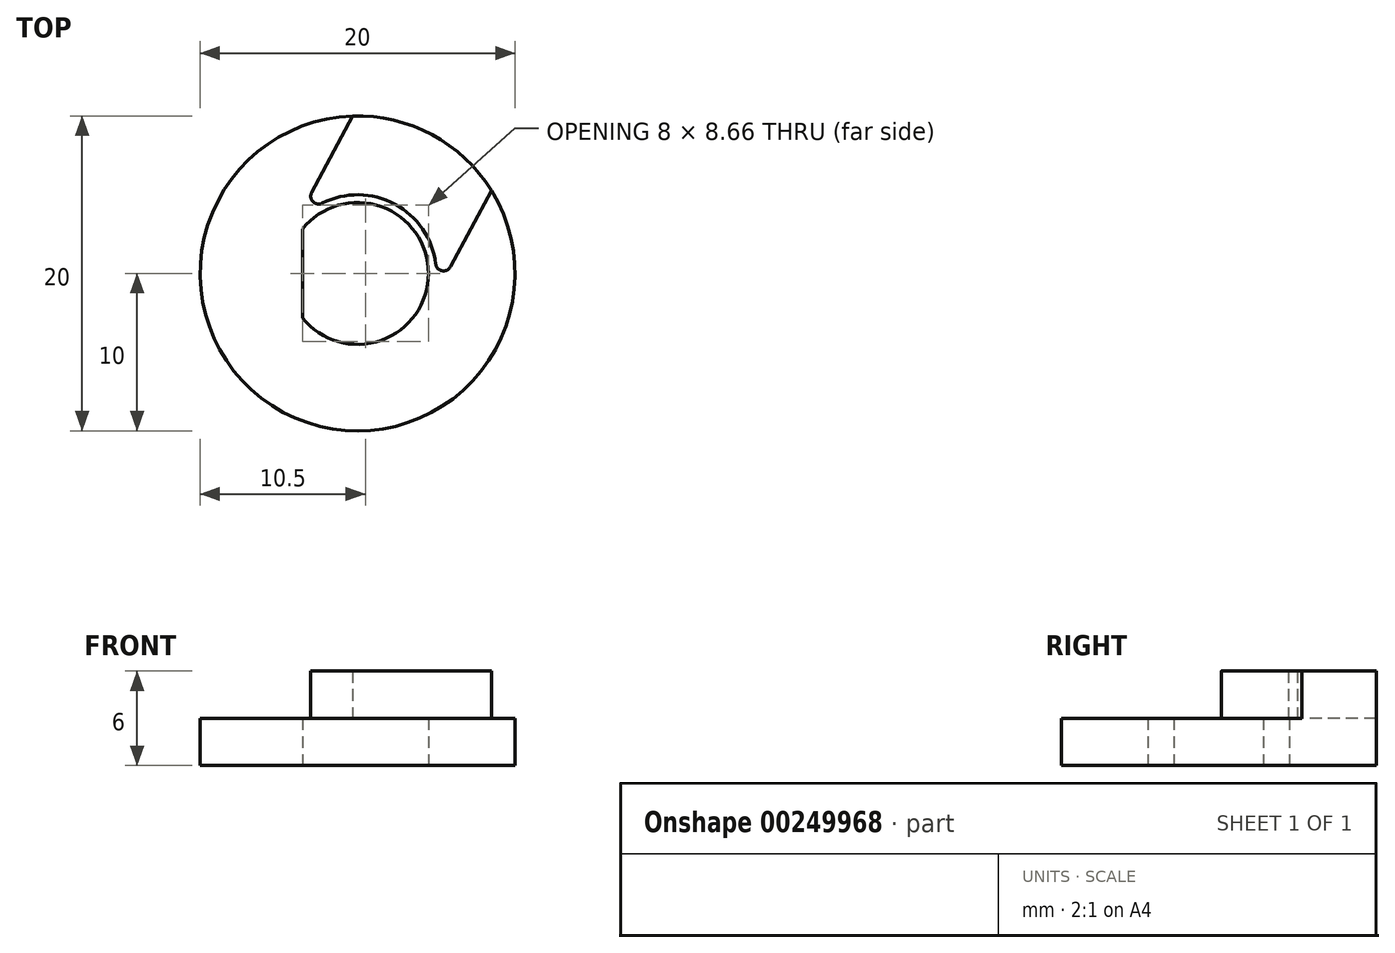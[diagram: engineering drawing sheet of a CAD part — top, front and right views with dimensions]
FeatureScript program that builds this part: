
annotation { "Feature Type Name" : "Feature", "Feature Type Description" : "" }
export const myFeature = defineFeature(function(context is Context, id is Id, definition is map)
    precondition{}
    {
        {
            var Q0;
            Q0=qCreatedBy(makeId("Top.planeOp"),FACE);
            var sketch = newSketch(context, id + "F0", { "sketchPlane" : qUnion([Q0])});
            skArc(sketch, "E0", {"start": v(-3.5, -2.83) * mm, "mid": v(4.5, 0) * mm, "end": v(-3.5, 2.83) * mm});
            skCircle(sketch, "E1", {"center": v(0, 0) * mm, "radius": 10 * mm});
            skLineSegment(sketch, "E2", {"start": v(-3.5, -2.83) * mm, "end": v(-3.5, 2.83) * mm});
            skPoint(sketch, "E3.start.orphan", {"position": v(4.5, 0) * mm});
            skArc(sketch, "E4", {"start": v(4.4, -2.36) * mm, "mid": v(2.36, 4.4) * mm, "end": v(-4.4, 2.36) * mm});
            skLineSegment(sketch, "E5", {"start": v(-4.4, 2.36) * mm, "end": v(-0.32, 10) * mm});
            skLineSegment(sketch, "E6", {"start": v(4.4, -2.36) * mm, "end": v(8.5, 5.28) * mm});
            skSolve(sketch);
        }
        {
            var Q0;
            Q0=makeQuery(id+"F0.imprint","IMPRINT",FACE,{"disambiguationData":[TD([[makeQuery(id+"F0.imprint","IMPRINT",EDGE,{"derivedFrom":sQuery(id+"F0.wireOp",EDGE,"E0")}),-1.0]])]});
            var Q1;
            Q1=makeQuery(id+"F0.imprint","IMPRINT",FACE,{"disambiguationData":[TD([[makeQuery(id+"F0.imprint","IMPRINT",EDGE,{"derivedFrom":sQuery(id+"F0.wireOp",EDGE,"E4")}),-1.0]])]});
            extrude(context, id + "F1", {"entities" : qUnion([Q0, Q1]), "depth" : 3 * mm});
        }
        {
            var Q0;
            Q0=makeQuery(id+"F0.imprint","IMPRINT",FACE,{"disambiguationData":[TD([[makeQuery(id+"F0.imprint","IMPRINT",EDGE,{"derivedFrom":sQuery(id+"F0.wireOp",EDGE,"E4")}),-1.0]])]});
            extrude(context, id + "F2", {"entities" : qUnion([Q0]), "operationType" : NewBodyOperationType.ADD, "depth" : 6 * mm});
        }
        {
            var Q0;
            Q0=makeQuery(id+"F2.opExtrude","SWEPT_EDGE",EDGE,{"disambiguationData":[OSD([sQuery(id+"F0.wireOp",EDGE,"E4"),sQuery(id+"F0.wireOp",EDGE,"E5")])]});
            var Q1;
            Q1=makeQuery(id+"F2.opExtrude","SWEPT_EDGE",EDGE,{"disambiguationData":[OSD([sQuery(id+"F0.wireOp",EDGE,"E4"),sQuery(id+"F0.wireOp",EDGE,"E6")])]});
            fillet(context, id + "F3", {"entities" : qUnion([Q0, Q1]), "radius" : 0.5 * mm, "tangentPropagation" : true, "allowEdgeOverflow" : false});
        }
    });
